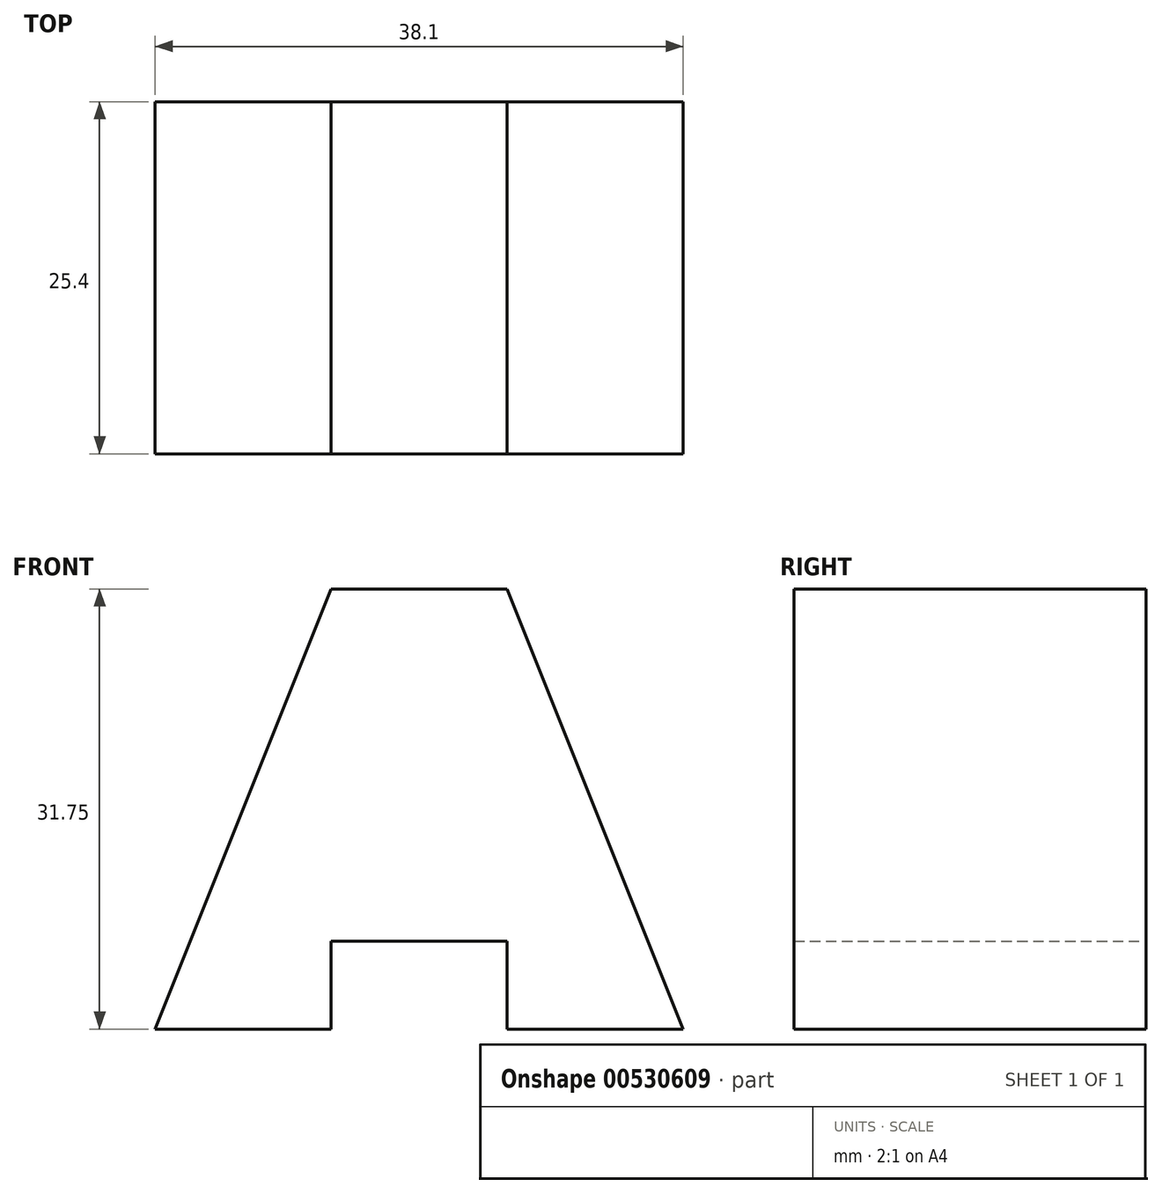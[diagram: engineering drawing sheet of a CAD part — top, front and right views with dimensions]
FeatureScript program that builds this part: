
annotation { "Feature Type Name" : "Feature", "Feature Type Description" : "" }
export const myFeature = defineFeature(function(context is Context, id is Id, definition is map)
    precondition{}
    {
        {
            var Q0;
            Q0=qCreatedBy(makeId("Front.planeOp"),FACE);
            var sketch = newSketch(context, id + "F0", { "sketchPlane" : qUnion([Q0])});
            skLineSegment(sketch, "E0", {"start": v(-61.86, 0.2) * mm, "end": v(-49.16, 0.2) * mm});
            skLineSegment(sketch, "E1", {"start": v(-49.16, 6.55) * mm, "end": v(-49.16, 0.2) * mm});
            skLineSegment(sketch, "E2", {"start": v(-49.16, 6.55) * mm, "end": v(-36.46, 6.55) * mm});
            skLineSegment(sketch, "E3", {"start": v(-36.46, 0.2) * mm, "end": v(-36.46, 6.55) * mm});
            skLineSegment(sketch, "E4", {"start": v(-36.46, 0.2) * mm, "end": v(-23.76, 0.2) * mm});
            skLineSegment(sketch, "E5", {"start": v(-23.76, 0.2) * mm, "end": v(-36.46, 31.95) * mm});
            skLineSegment(sketch, "E6", {"start": v(-36.46, 31.95) * mm, "end": v(-49.16, 31.95) * mm});
            skLineSegment(sketch, "E7", {"start": v(-49.16, 31.95) * mm, "end": v(-61.86, 0.2) * mm});
            skSolve(sketch);
        }
        {
            var Q0;
            Q0 = qSketchRegion(id + "F0", true);
            extrude(context, id + "F1", {"entities" : qUnion([Q0]), "depth" : 25.4 * mm, "offsetDistance" : 25.4 * mm});
        }
    });
